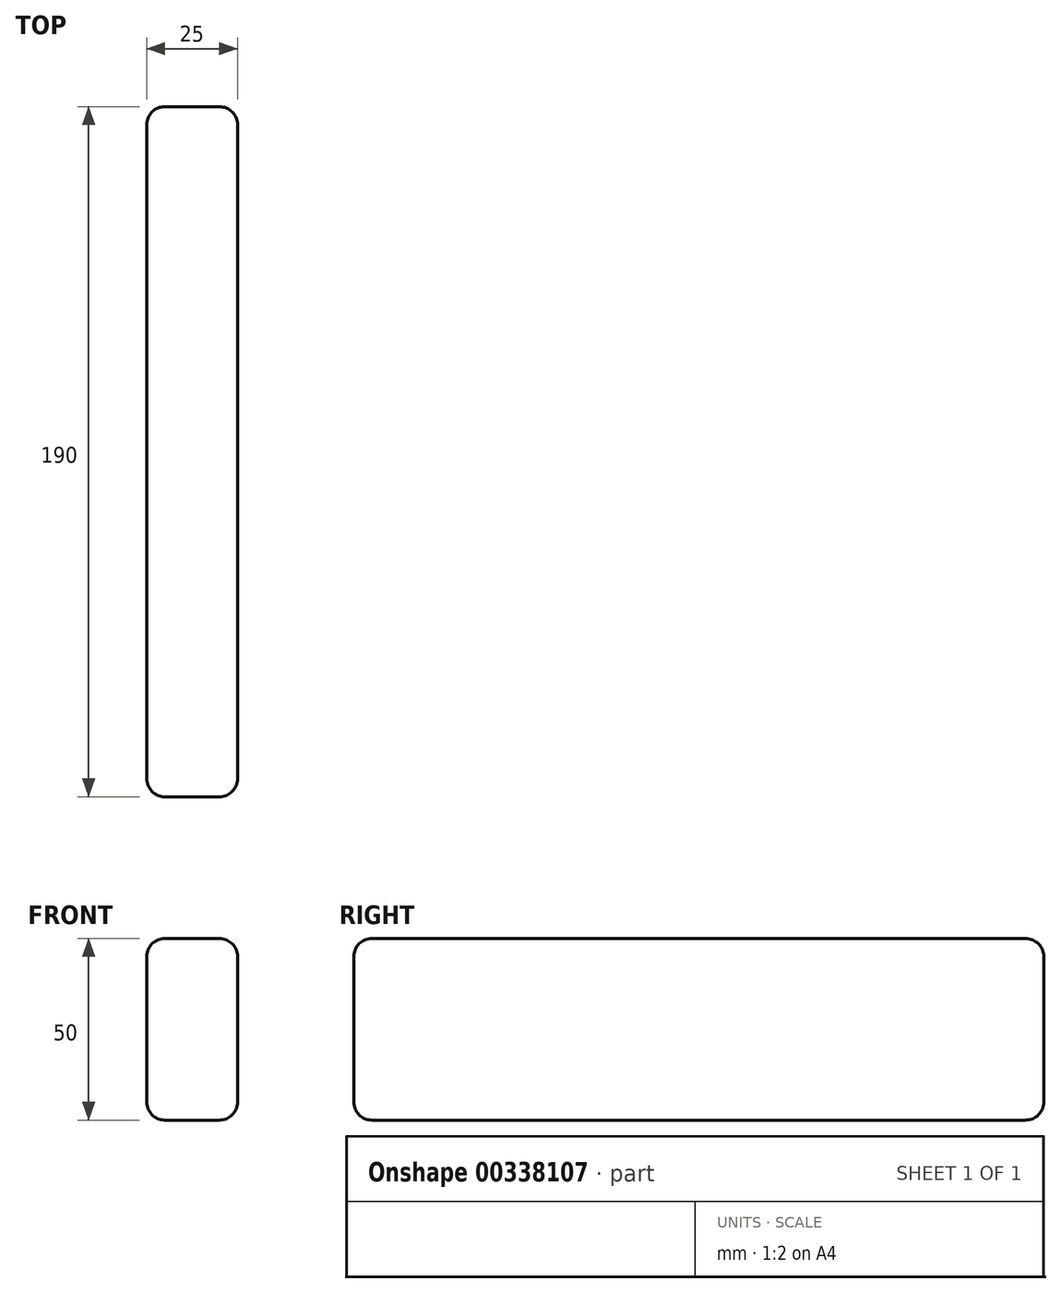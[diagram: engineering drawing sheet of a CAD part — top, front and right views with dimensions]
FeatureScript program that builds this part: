
annotation { "Feature Type Name" : "Feature", "Feature Type Description" : "" }
export const myFeature = defineFeature(function(context is Context, id is Id, definition is map)
    precondition{}
    {
        {
            var Q0;
            Q0=qCreatedBy(makeId("Front.planeOp"),FACE);
            var sketch = newSketch(context, id + "F0", { "sketchPlane" : qUnion([Q0])});
            skLineSegment(sketch, "E0.bottom", {"start": v(25, 50) * mm, "end": v(0, 50) * mm});
            skLineSegment(sketch, "E0.top", {"start": v(25, 0) * mm, "end": v(0, 0) * mm});
            skLineSegment(sketch, "E0.left", {"start": v(25, 50) * mm, "end": v(25, 0) * mm});
            skLineSegment(sketch, "E0.right", {"start": v(0, 50) * mm, "end": v(0, 0) * mm});
            skSolve(sketch);
        }
        {
            var Q0;
            Q0 = qSketchRegion(id + "F0", true);
            extrude(context, id + "F1", {"entities" : qUnion([Q0]), "depth" : 190 * mm});
        }
        {
            var Q0;
            Q0=makeQuery(id+"F1.opExtrude","CAP_FACE",FACE,{"disambiguationData":[OSD([sQuery(id+"F0.wireOp",EDGE,"E0.bottom"),sQuery(id+"F0.wireOp",EDGE,"E0.top"),sQuery(id+"F0.wireOp",EDGE,"E0.left"),sQuery(id+"F0.wireOp",EDGE,"E0.right")])],"isStart":false});
            var Q1;
            {var subQ0=sQuery(id+"F0.wireOp",EDGE,"E0.bottom");Q1=makeQuery(id+"F9xLpaGY6Voh3Az_1.opFillet","BLEND_EDGE",EDGE,{"blendedFrom":[makeQuery(id+"F1.opExtrude","SWEPT_EDGE",EDGE,{"disambiguationData":[OSD([subQ0,sQuery(id+"F0.wireOp",EDGE,"E0.left")])]}),makeQuery(id+"F1.opExtrude","SWEPT_FACE",FACE,{"disambiguationData":[OSD([subQ0])]})],"blendedInto":[makeQuery(id+"F1.opExtrude","SWEPT_FACE",FACE,{"disambiguationData":[OSD([subQ0])]})]});}
            var Q2;
            Q2=makeQuery(id+"F1.opExtrude","SWEPT_EDGE",EDGE,{"disambiguationData":[OSD([sQuery(id+"F0.wireOp",EDGE,"E0.bottom"),sQuery(id+"F0.wireOp",EDGE,"E0.right")])]});
            var Q3;
            Q3=makeQuery(id+"F1.opExtrude","CAP_EDGE",EDGE,{"disambiguationData":[OSD([sQuery(id+"F0.wireOp",EDGE,"E0.bottom")])],"isStart":true});
            var Q4;
            Q4=makeQuery(id+"F1.opExtrude","SWEPT_EDGE",EDGE,{"disambiguationData":[OSD([sQuery(id+"F0.wireOp",EDGE,"E0.top"),sQuery(id+"F0.wireOp",EDGE,"E0.left")])]});
            var Q5;
            Q5=makeQuery(id+"F1.opExtrude","SWEPT_EDGE",EDGE,{"disambiguationData":[OSD([sQuery(id+"F0.wireOp",EDGE,"E0.top"),sQuery(id+"F0.wireOp",EDGE,"E0.right")])]});
            var Q6;
            Q6=makeQuery(id+"F1.opExtrude","CAP_EDGE",EDGE,{"disambiguationData":[OSD([sQuery(id+"F0.wireOp",EDGE,"E0.top")])],"isStart":true});
            var Q7;
            Q7=makeQuery(id+"F1.opExtrude","SWEPT_EDGE",EDGE,{"disambiguationData":[OSD([sQuery(id+"F0.wireOp",EDGE,"E0.bottom"),sQuery(id+"F0.wireOp",EDGE,"E0.left")])]});
            var Q8;
            Q8=makeQuery(id+"F1.opExtrude","CAP_EDGE",EDGE,{"disambiguationData":[OSD([sQuery(id+"F0.wireOp",EDGE,"E0.right")])],"isStart":true});
            var Q9;
            Q9=makeQuery(id+"F1.opExtrude","CAP_EDGE",EDGE,{"disambiguationData":[OSD([sQuery(id+"F0.wireOp",EDGE,"E0.left")])],"isStart":true});
            fillet(context, id + "F2", {"entities" : qUnion([Q0, Q1, Q2, Q3, Q4, Q5, Q6, Q7, Q8, Q9]), "radius" : 5 * mm, "tangentPropagation" : true, "allowEdgeOverflow" : false});
        }
    });
